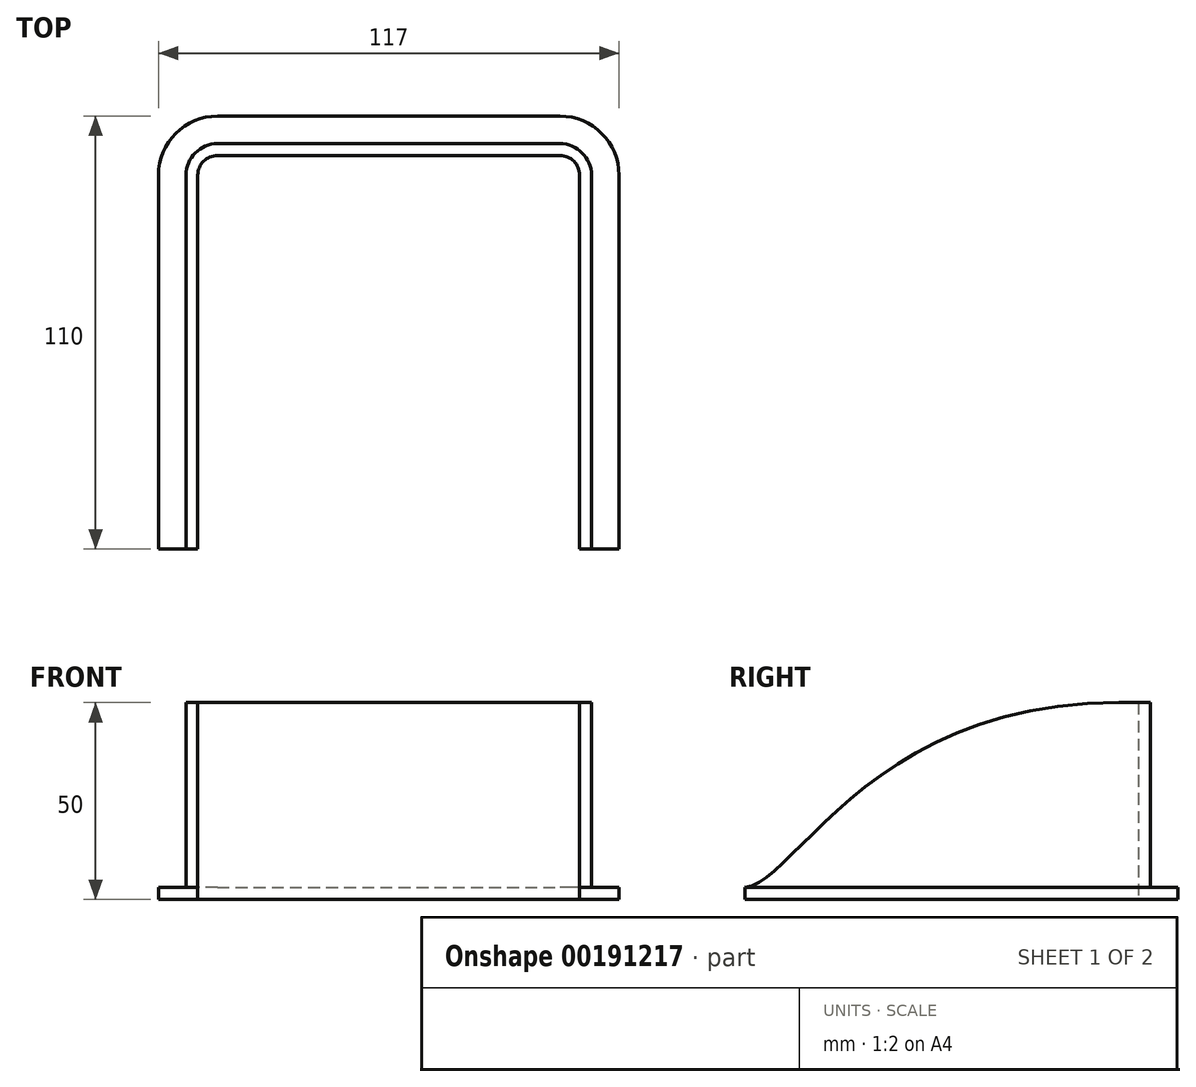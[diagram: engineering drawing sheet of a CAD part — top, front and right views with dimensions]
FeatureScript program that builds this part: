
annotation { "Feature Type Name" : "Feature", "Feature Type Description" : "" }
export const myFeature = defineFeature(function(context is Context, id is Id, definition is map)
    precondition{}
    {
        {
            var Q0;
            Q0=qCreatedBy(makeId("Top.planeOp"),FACE);
            var sketch = newSketch(context, id + "F0", { "sketchPlane" : qUnion([Q0])});
            skLineSegment(sketch, "E0", {"start": v(-48.5, 0) * mm, "end": v(-48.5, 95) * mm});
            skLineSegment(sketch, "E1", {"start": v(-43.5, 100) * mm, "end": v(43.5, 100) * mm});
            skLineSegment(sketch, "E2", {"start": v(48.5, 95) * mm, "end": v(48.5, 0) * mm});
            skPoint(sketch, "E3.visualSharp", {"position": v(-48.5, 100) * mm});
            skArc(sketch, "E3.filletArc", {"start": v(-43.5, 100) * mm, "mid": v(-47.04, 98.54) * mm, "end": v(-48.5, 95) * mm});
            skPoint(sketch, "E4.visualSharp", {"position": v(48.5, 100) * mm});
            skArc(sketch, "E4.filletArc", {"start": v(48.5, 95) * mm, "mid": v(47.04, 98.54) * mm, "end": v(43.5, 100) * mm});
            skLineSegment(sketch, "E5.0", {"start": v(58.5, 95) * mm, "end": v(58.5, 0) * mm});
            skLineSegment(sketch, "E5.1", {"start": v(-58.5, 0) * mm, "end": v(-58.5, 95) * mm});
            skArc(sketch, "E5.2", {"start": v(-43.5, 110) * mm, "mid": v(-54.1, 105.6) * mm, "end": v(-58.5, 95) * mm});
            skLineSegment(sketch, "E5.3", {"start": v(-43.5, 110) * mm, "end": v(43.5, 110) * mm});
            skArc(sketch, "E5.4", {"start": v(58.5, 95) * mm, "mid": v(54.1, 105.6) * mm, "end": v(43.5, 110) * mm});
            skLineSegment(sketch, "E6.0", {"start": v(51.5, 95) * mm, "end": v(51.5, 0) * mm});
            skLineSegment(sketch, "E6.1", {"start": v(-51.5, 0) * mm, "end": v(-51.5, 95) * mm});
            skArc(sketch, "E6.2", {"start": v(-43.5, 103) * mm, "mid": v(-49.16, 100.66) * mm, "end": v(-51.5, 95) * mm});
            skLineSegment(sketch, "E6.3", {"start": v(-43.5, 103) * mm, "end": v(43.5, 103) * mm});
            skArc(sketch, "E6.4", {"start": v(51.5, 95) * mm, "mid": v(49.16, 100.66) * mm, "end": v(43.5, 103) * mm});
            skLineSegment(sketch, "E7", {"start": v(-51.5, 0) * mm, "end": v(-48.5, 0) * mm});
            skLineSegment(sketch, "E8", {"start": v(-58.5, 0) * mm, "end": v(-51.5, 0) * mm});
            skLineSegment(sketch, "E9", {"start": v(48.5, 0) * mm, "end": v(51.5, 0) * mm});
            skLineSegment(sketch, "E10", {"start": v(51.5, 0) * mm, "end": v(58.5, 0) * mm});
            skSolve(sketch);
        }
        {
            var Q0;
            Q0=makeQuery(id+"F0.imprint","IMPRINT",FACE,{"disambiguationData":[TD([[makeQuery(id+"F0.imprint","IMPRINT",EDGE,{"derivedFrom":sQuery(id+"F0.wireOp",EDGE,"E0")}),1.0]])]});
            extrude(context, id + "F1", {"entities" : qUnion([Q0]), "depth" : 50 * mm});
        }
        {
            var Q0;
            Q0=makeQuery(id+"F0.imprint","IMPRINT",FACE,{"disambiguationData":[TD([[makeQuery(id+"F0.imprint","IMPRINT",EDGE,{"derivedFrom":sQuery(id+"F0.wireOp",EDGE,"E5.0")}),-1.0]])]});
            extrude(context, id + "F2", {"entities" : qUnion([Q0]), "operationType" : NewBodyOperationType.ADD, "depth" : 3 * mm});
        }
        {
            var Q0;
            Q0=makeQuery(id+"F1.opExtrude","SWEPT_FACE",FACE,{"disambiguationData":[OSD([sQuery(id+"F0.wireOp",EDGE,"E6.1")])]});
            var sketch = newSketch(context, id + "F3", { "sketchPlane" : qUnion([Q0])});
            skFitSpline(sketch, "E11", {"points": [v(-95, 50) * mm, v(0, 3) * mm], "startDerivative": vector(189.93, 0) * mm, "endDerivative": vector(38.81, -4.03) * mm});
            skSolve(sketch);
        }
        {
            var Q0;
            Q0=makeQuery(id+"F3.imprint","IMPRINT",FACE,{"disambiguationData":[TD([[makeQuery(id+"F3.imprint","IMPRINT",EDGE,{"derivedFrom":sQuery(id+"F3.wireOp",EDGE,"E11")}),1.0]])]});
            var Q1;
            Q1=makeQuery(id+"F1.opExtrude","SWEPT_FACE",FACE,{"disambiguationData":[OSD([sQuery(id+"F0.wireOp",EDGE,"E6.0")])]});
            extrude(context, id + "F4", {"entities" : qUnion([Q0]), "operationType" : NewBodyOperationType.REMOVE, "endBound" : BoundingType.UP_TO_SURFACE, "oppositeDirection" : true, "endBoundEntityFace" : qUnion([Q1]), "depth" : 25 * mm});
        }
    });
